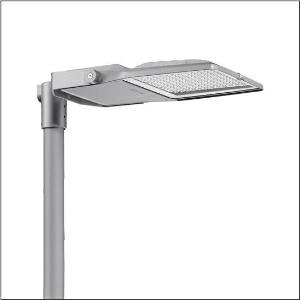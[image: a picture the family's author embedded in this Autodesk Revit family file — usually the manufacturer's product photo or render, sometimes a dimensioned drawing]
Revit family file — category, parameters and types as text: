
# Revit family: floodlight_fl_21_midi___pl52_5xa7786e2d3a_7127
name_source: partatom
category: Lighting Fixtures
units: mm (PartAtom-declared; Revit-internal decimal feet)

## family parameters
Cut with Voids When Loaded = No
Host = Face
Light Source = No
Part Type = Normal
Room Calculation Point = No
Round Connector Dimension = Use Diameter
Shared = No

## types (1)
- --- (1 x LED, 26940 lm, 212.4 W, 3000K)
    Apparent Load = 212 VA
    CIE Flux Codes = 26 60 98 100 100
    Color Rendering = 70
    Color Temperature = 3000K
    Default Elevation = 1800 mm
    Description = Floodlight FL 21 midi, floodlight, primary light control with lens, of PMMA, primary optical cover: protective disc, of toughened safety glass, transparent, light distribution: PL52, light emission: direct distribution, installation type: surface-mounted, LED, High Power LED, rated luminous flux: 26.940lm, luminous efficacy: 127lm/W, light colour: 730, colour temperature: 3000K, control gear: ECG Smart Interface, control: flexible luminous flux parameterisation, time-dependent luminous flux control, constant luminous flux control, overheat protection, presetting dimming logarithmic, with terminal, 6-pole, mains connection: 220..240V, AC, 50/60Hz, start of lifetime: 212W, end of service life: 231W, reduction: 95W, luminaire housing, of diecast aluminium, powder-coated, Siteco® metallic grey (DB 702S), corrosivity category C5 mid according to DIN EN ISO 12944, sealing non-destructively replaceable, please order mast flange separately, mast bracket, of steel, galvanised, powder-coated, Siteco® metallic grey (DB 702S), Smart Interface below and above, protection rating (complete): IP66, insulation class (complete): insulation class II (safety insulation), certification: CE, protection symbol: D, impact resistance: IK08, permissible operating ambient temperature: -40..+40°C, permissible operating ambient temperature for outdoor applications: -40..+50°C, standard: DIN EN 12944, LABS conformity tested according to VDMA 24364:2018-05, packaging unit: 1 piece

Light Distribution: PL52
    Height = 76 mm
    Lamp = 1 x LED
    Lamp Light Flux = 26940 lm
    Lamp Power = 212.4 W
    Lamp count = 1
    Length = 657 mm
    Luminous efficacy = 127 lm/W
    Manufacturer = Siteco
    ModVariant = No
    Model = 5XA7786E2D3A
    Number of Poles = 1
    OnlyDefault = Yes
    Power Factor = 1
    Product Name = Floodlight FL 21 midi | PL52
    Product group = floodlight | pylon annexe
    ProductGroupID = 6200
    Protection Class = Protection class II
    Protection Degree = IP 66
    RLX_Detail_Level = 1
    RLX_Emergency_Light_Flux = 0 lm
    RLX_Emergency_Type = 0
    RLX_Emergency_Type_DB = No
    RlxData = <blob elided: 153953 chars, md5=a220a232>
    Socket = socket
    Standby Power = 0 W
    System Light Flux = 26940 lm
    System Power = 212 W
    Type Comments = factory setting: luminous flux: 100 % | dim-lin: 254 | 710 mA
    Type Image = l_1007123.jpg
    URL = http://relux.com
    VarID = @adj_128739
    Voltage = 0 V
    Weight = 0.00 kg
    Width = 442 mm

## geometry (parser evidence)
native form markers: Blend x4, Sweep x13
no freeform markers — native parametric forms only
